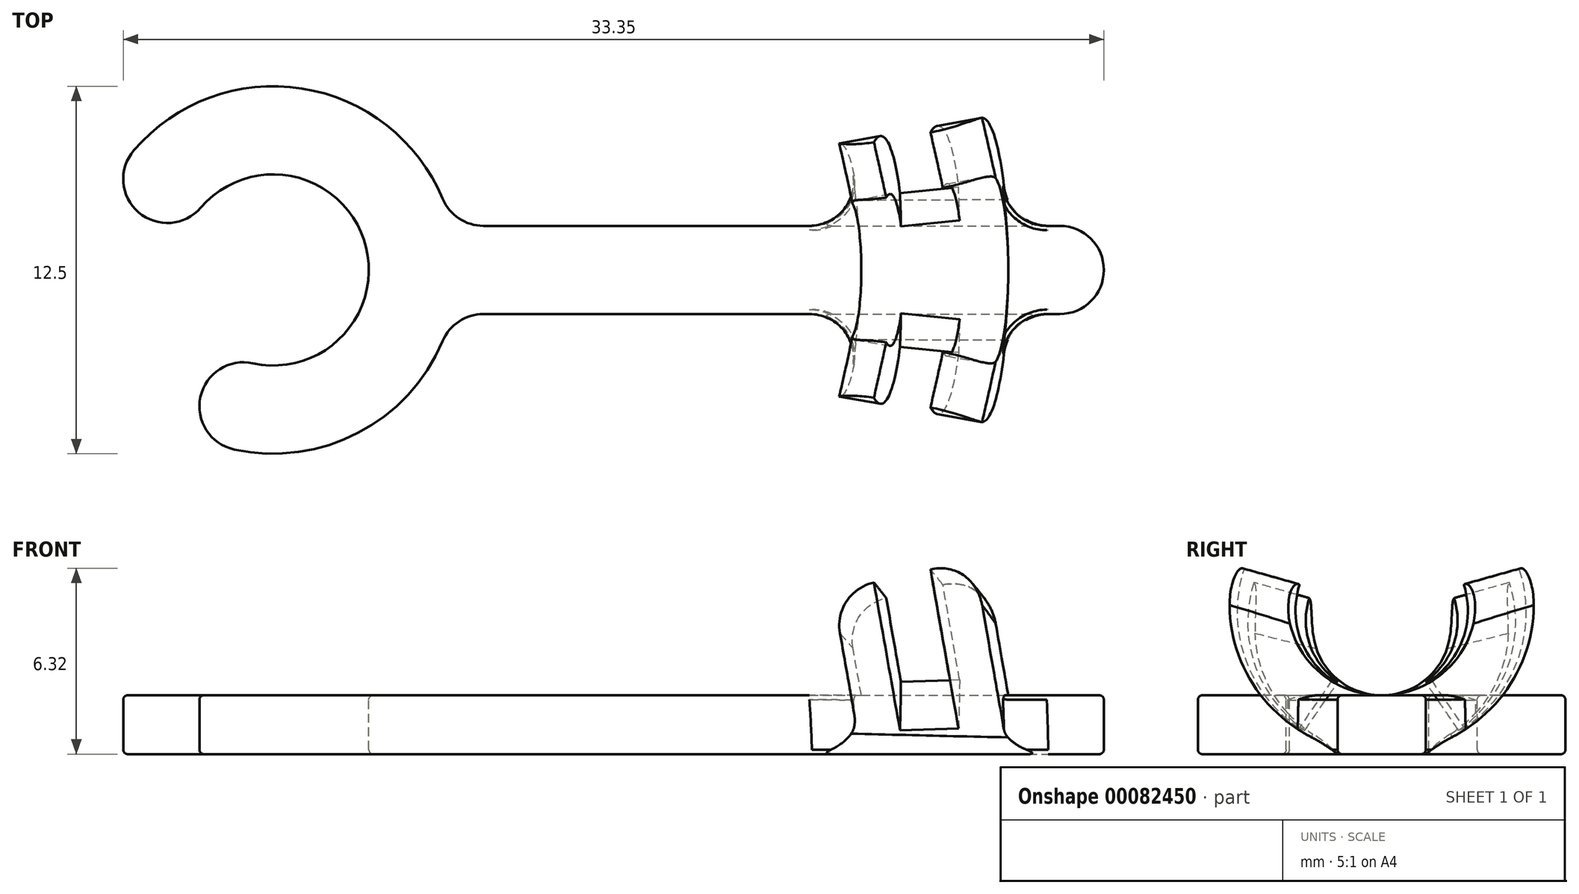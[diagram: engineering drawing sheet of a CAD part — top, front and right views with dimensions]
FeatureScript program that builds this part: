
annotation { "Feature Type Name" : "Feature", "Feature Type Description" : "" }
export const myFeature = defineFeature(function(context is Context, id is Id, definition is map)
    precondition{}
    {
        {
            var Q0;
            Q0=qCreatedBy(makeId("Top.planeOp"),FACE);
            var sketch = newSketch(context, id + "F0", { "sketchPlane" : qUnion([Q0])});
            skLineSegment(sketch, "E0.bottom", {"start": v(0, -1.5) * mm, "end": v(25, -1.5) * mm});
            skLineSegment(sketch, "E0.top", {"start": v(0, 1.5) * mm, "end": v(25, 1.5) * mm});
            skLineSegment(sketch, "E0.left", {"start": v(0, -1.5) * mm, "end": v(0, 1.5) * mm});
            skLineSegment(sketch, "E0.right", {"start": v(25, -1.5) * mm, "end": v(25, 1.5) * mm});
            skSolve(sketch);
        }
        {
            var Q0;
            Q0 = qSketchRegion(id + "F0", true);
            extrude(context, id + "F1", {"entities" : qUnion([Q0]), "depth" : 2 * mm});
        }
        {
            var Q0;
            Q0=qCreatedBy(makeId("Front.planeOp"),FACE);
            var sketch = newSketch(context, id + "F2", { "sketchPlane" : qUnion([Q0])});
            skLineSegment(sketch, "E1.bottom", {"start": v(0, 0) * mm, "end": v(3, 0) * mm});
            skLineSegment(sketch, "E1.top", {"start": v(0, 2) * mm, "end": v(3, 2) * mm});
            skLineSegment(sketch, "E1.left", {"start": v(0, 0) * mm, "end": v(0, 2) * mm});
            skLineSegment(sketch, "E1.right", {"start": v(3, 0) * mm, "end": v(3, 2) * mm});
            skLineSegment(sketch, "E2", {"start": v(-3.25, 5.83) * mm, "end": v(-3.25, -3) * mm});
            skSolve(sketch);
        }
        {
            var Q0;
            Q0=makeQuery(id+"F2.imprint","IMPRINT",FACE,{"disambiguationData":[TD([[makeQuery(id+"F2.imprint","IMPRINT",EDGE,{"derivedFrom":sQuery(id+"F2.wireOp",EDGE,"E1.bottom")}),1.0]])]});
            var Q1;
            Q1=sQuery(id+"F2.wireOp",EDGE,"E2");
            revolve(context, id + "F3", {"operationType" : NewBodyOperationType.ADD, "entities" : qUnion([Q0]), "axis" : qUnion([Q1]), "revolveType" : RevolveType.TWO_DIRECTIONS, "angle" : 120.7 * degree, "angleBack" : 202.27 * degree});
        }
        {
            var Q0;
            Q0=qCreatedBy(makeId("Front.planeOp"),FACE);
            var sketch = newSketch(context, id + "F4", { "sketchPlane" : qUnion([Q0])});
            skLineSegment(sketch, "E3.bottom", {"start": v(21.75, 0) * mm, "end": v(16.75, 0) * mm});
            skLineSegment(sketch, "E3.top", {"start": v(21.75, 2) * mm, "end": v(16.75, 2) * mm});
            skLineSegment(sketch, "E3.left", {"start": v(21.75, 0) * mm, "end": v(21.75, 2) * mm});
            skLineSegment(sketch, "E3.right", {"start": v(16.75, 0) * mm, "end": v(16.75, 2) * mm});
            skLineSegment(sketch, "E4", {"start": v(14.65, 4) * mm, "end": v(25.16, 5.85) * mm});
            skSolve(sketch);
        }
        {
            var Q0;
            Q0=makeQuery(id+"F4.imprint","IMPRINT",FACE,{"disambiguationData":[TD([[makeQuery(id+"F4.imprint","IMPRINT",EDGE,{"derivedFrom":sQuery(id+"F4.wireOp",EDGE,"E3.bottom")}),-1.0]])]});
            var Q1;
            Q1=sQuery(id+"F4.wireOp",EDGE,"E4");
            revolve(context, id + "F5", {"operationType" : NewBodyOperationType.ADD, "entities" : qUnion([Q0]), "axis" : qUnion([Q1]), "revolveType" : RevolveType.SYMMETRIC, "angle" : 215 * degree});
        }
        {
            var Q0;
            Q0=makeQuery(id+"F3.boolean.opBoolean","INTERSECT",EDGE,{"derivedFrom":[makeQuery(id+"F1.opExtrude","SWEPT_FACE",FACE,{"disambiguationData":[OSD([sQuery(id+"F0.wireOp",EDGE,"E0.bottom")])]}),makeQuery(id+"F3.opRevolve","SWEPT_FACE",FACE,{"disambiguationData":[OSD([sQuery(id+"F2.wireOp",EDGE,"E1.right")])]})]});
            var Q1;
            Q1=makeQuery(id+"F3.boolean.opBoolean","INTERSECT",EDGE,{"derivedFrom":[makeQuery(id+"F1.opExtrude","SWEPT_FACE",FACE,{"disambiguationData":[OSD([sQuery(id+"F0.wireOp",EDGE,"E0.top")])]}),makeQuery(id+"F3.opRevolve","SWEPT_FACE",FACE,{"disambiguationData":[OSD([sQuery(id+"F2.wireOp",EDGE,"E1.right")])]})]});
            var Q2;
            Q2=makeQuery(id+"F3.opRevolve","CAP_EDGE",EDGE,{"disambiguationData":[OSD([sQuery(id+"F2.wireOp",EDGE,"E1.right")])],"isStart":false});
            var Q3;
            Q3=makeQuery(id+"F3.opRevolve","CAP_EDGE",EDGE,{"disambiguationData":[OSD([sQuery(id+"F2.wireOp",EDGE,"E1.left")])],"isStart":false});
            var Q4;
            Q4=makeQuery(id+"F3.opRevolve","CAP_EDGE",EDGE,{"disambiguationData":[OSD([sQuery(id+"F2.wireOp",EDGE,"E1.left")])],"isStart":true});
            var Q5;
            Q5=makeQuery(id+"F3.opRevolve","CAP_EDGE",EDGE,{"disambiguationData":[OSD([sQuery(id+"F2.wireOp",EDGE,"E1.right")])],"isStart":true});
            var Q6;
            Q6=makeQuery(id+"F1.opExtrude","SWEPT_EDGE",EDGE,{"disambiguationData":[OSD([sQuery(id+"F0.wireOp",EDGE,"E0.top"),sQuery(id+"F0.wireOp",EDGE,"E0.right")])]});
            var Q7;
            Q7=makeQuery(id+"F1.opExtrude","SWEPT_EDGE",EDGE,{"disambiguationData":[OSD([sQuery(id+"F0.wireOp",EDGE,"E0.bottom"),sQuery(id+"F0.wireOp",EDGE,"E0.right")])]});
            var Q8;
            Q8=makeQuery(id+"F5.opRevolve","CAP_EDGE",EDGE,{"disambiguationData":[OSD([sQuery(id+"F4.wireOp",EDGE,"E3.right")])],"isStart":true});
            var Q9;
            Q9=makeQuery(id+"F5.opRevolve","CAP_EDGE",EDGE,{"disambiguationData":[OSD([sQuery(id+"F4.wireOp",EDGE,"E3.left")])],"isStart":true});
            var Q10;
            Q10=makeQuery(id+"F5.opRevolve","CAP_EDGE",EDGE,{"disambiguationData":[OSD([sQuery(id+"F4.wireOp",EDGE,"E3.right")])],"isStart":false});
            var Q11;
            Q11=makeQuery(id+"F5.opRevolve","CAP_EDGE",EDGE,{"disambiguationData":[OSD([sQuery(id+"F4.wireOp",EDGE,"E3.left")])],"isStart":false});
            var Q12;
            Q12=makeQuery(id+"F5.boolean.opBoolean","INTERSECT",EDGE,{"derivedFrom":[makeQuery(id+"F1.opExtrude","SWEPT_FACE",FACE,{"disambiguationData":[OSD([sQuery(id+"F0.wireOp",EDGE,"E0.bottom")])]}),makeQuery(id+"F5.opRevolve","SWEPT_FACE",FACE,{"disambiguationData":[OSD([sQuery(id+"F4.wireOp",EDGE,"E3.left")])]})]});
            var Q13;
            Q13=makeQuery(id+"F5.boolean.opBoolean","INTERSECT",EDGE,{"derivedFrom":[makeQuery(id+"F1.opExtrude","SWEPT_FACE",FACE,{"disambiguationData":[OSD([sQuery(id+"F0.wireOp",EDGE,"E0.top")])]}),makeQuery(id+"F5.opRevolve","SWEPT_FACE",FACE,{"disambiguationData":[OSD([sQuery(id+"F4.wireOp",EDGE,"E3.left")])]})]});
            var Q14;
            Q14=makeQuery(id+"F5.boolean.opBoolean","INTERSECT",EDGE,{"derivedFrom":[makeQuery(id+"F1.opExtrude","SWEPT_FACE",FACE,{"disambiguationData":[OSD([sQuery(id+"F0.wireOp",EDGE,"E0.bottom")])]}),makeQuery(id+"F5.opRevolve","SWEPT_FACE",FACE,{"disambiguationData":[OSD([sQuery(id+"F4.wireOp",EDGE,"E3.right")])]})]});
            var Q15;
            Q15=makeQuery(id+"F5.boolean.opBoolean","INTERSECT",EDGE,{"derivedFrom":[makeQuery(id+"F1.opExtrude","SWEPT_FACE",FACE,{"disambiguationData":[OSD([sQuery(id+"F0.wireOp",EDGE,"E0.top")])]}),makeQuery(id+"F5.opRevolve","SWEPT_FACE",FACE,{"disambiguationData":[OSD([sQuery(id+"F4.wireOp",EDGE,"E3.right")])]})]});
            fillet(context, id + "F6", {"entities" : qUnion([Q0, Q1, Q2, Q3, Q4, Q5, Q6, Q7, Q8, Q9, Q10, Q11, Q12, Q13, Q14, Q15]), "radius" : 1.5 * mm, "tangentPropagation" : true, "allowEdgeOverflow" : false});
        }
        {
            var Q0;
            Q0=makeQuery(id+"F5.boolean.opBoolean","INTERSECT",EDGE,{"derivedFrom":[makeQuery(id+"F1.opExtrude","SWEPT_FACE",FACE,{"disambiguationData":[OSD([sQuery(id+"F0.wireOp",EDGE,"E0.bottom")])]}),makeQuery(id+"F5.opRevolve","SWEPT_FACE",FACE,{"disambiguationData":[OSD([sQuery(id+"F4.wireOp",EDGE,"E3.bottom")])]})]});
            var Q1;
            Q1=makeQuery(id+"F5.boolean.opBoolean","INTERSECT",EDGE,{"derivedFrom":[makeQuery(id+"F1.opExtrude","SWEPT_FACE",FACE,{"disambiguationData":[OSD([sQuery(id+"F0.wireOp",EDGE,"E0.top")])]}),makeQuery(id+"F5.opRevolve","SWEPT_FACE",FACE,{"disambiguationData":[OSD([sQuery(id+"F4.wireOp",EDGE,"E3.bottom")])]})]});
            fillet(context, id + "F7", {"entities" : qUnion([Q0, Q1]), "radius" : 5 * mm, "tangentPropagation" : true, "allowEdgeOverflow" : false});
        }
        {
            var Q0;
            Q0=makeQuery(id+"F1.opExtrude","CAP_EDGE",EDGE,{"disambiguationData":[OSD([sQuery(id+"F0.wireOp",EDGE,"E0.bottom")])],"isStart":true});
            var Q1;
            {var subQ0=sQuery(id+"F0.wireOp",EDGE,"E0.right");var subQ1=sQuery(id+"F0.wireOp",EDGE,"E0.top");Q1=makeQuery(id+"F5.boolean.opBoolean","SPLIT",EDGE,{"disambiguationData":[TD([makeQuery(id+"F1.opExtrude","SWEPT_FACE",FACE,{"disambiguationData":[OSD([subQ0])]})])],"derivedFrom":makeQuery(id+"F1.opExtrude","CAP_EDGE",EDGE,{"disambiguationData":[OSD([subQ1])],"isStart":false})});}
            var Q2;
            {var subQ0=sQuery(id+"F0.wireOp",EDGE,"E0.top");Q2=makeQuery(id+"F5.boolean.opBoolean","SPLIT",EDGE,{"disambiguationData":[TD([makeQuery(id+"F3.opRevolve","SWEPT_FACE",FACE,{"disambiguationData":[OSD([sQuery(id+"F2.wireOp",EDGE,"E1.right")])]})])],"derivedFrom":makeQuery(id+"F1.opExtrude","CAP_EDGE",EDGE,{"disambiguationData":[OSD([subQ0])],"isStart":false})});}
            fillet(context, id + "F8", {"entities" : qUnion([Q0, Q1, Q2]), "radius" : .15 * mm, "tangentPropagation" : true, "allowEdgeOverflow" : false});
        }
        {
            var Q0;
            Q0=makeQuery(id+"F5.opRevolve","CAP_FACE",FACE,{"disambiguationData":[OSD([sQuery(id+"F4.wireOp",EDGE,"E3.bottom"),sQuery(id+"F4.wireOp",EDGE,"E3.top"),sQuery(id+"F4.wireOp",EDGE,"E3.left"),sQuery(id+"F4.wireOp",EDGE,"E3.right")])],"isStart":false});
            var Q1;
            Q1=makeQuery(id+"F5.opRevolve","CAP_FACE",FACE,{"disambiguationData":[OSD([sQuery(id+"F4.wireOp",EDGE,"E3.bottom"),sQuery(id+"F4.wireOp",EDGE,"E3.top"),sQuery(id+"F4.wireOp",EDGE,"E3.left"),sQuery(id+"F4.wireOp",EDGE,"E3.right")])],"isStart":true});
            var Q2;
            Q2=sQuery(id+"F4.wireOp",EDGE,"E4");
            revolve(context, id + "F9", {"operationType" : NewBodyOperationType.REMOVE, "entities" : qUnion([Q0, Q1]), "axis" : qUnion([Q2]), "revolveType" : RevolveType.SYMMETRIC, "oppositeDirection" : true, "angle" : 145 * degree});
        }
    });
